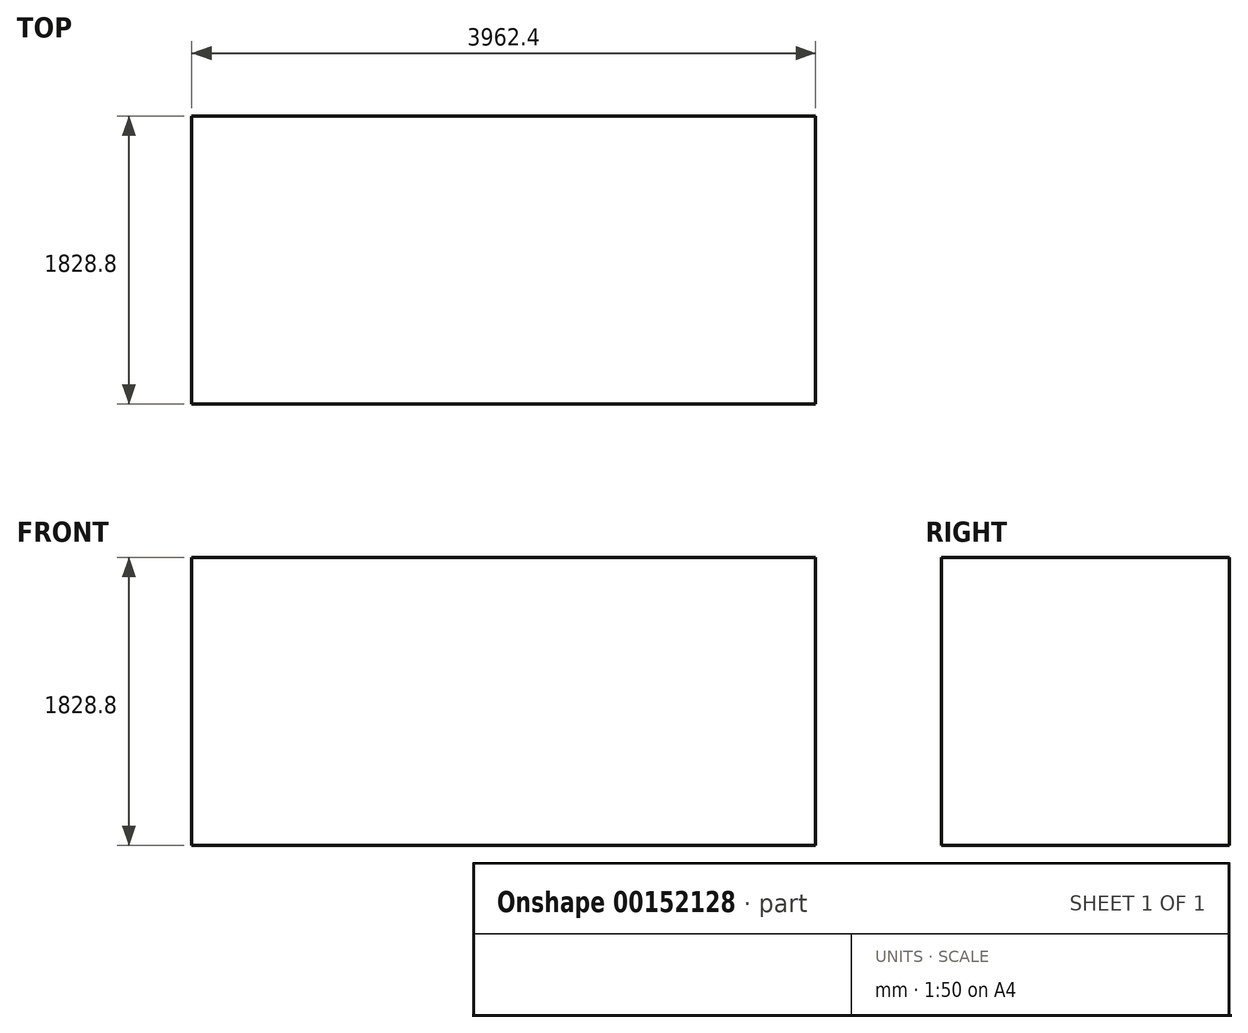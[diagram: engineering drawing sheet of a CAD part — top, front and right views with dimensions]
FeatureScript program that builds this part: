
annotation { "Feature Type Name" : "Feature", "Feature Type Description" : "" }
export const myFeature = defineFeature(function(context is Context, id is Id, definition is map)
    precondition{}
    {
        {
            var Q0;
            Q0=qCreatedBy(makeId("Top.planeOp"),FACE);
            var sketch = newSketch(context, id + "F0", { "sketchPlane" : qUnion([Q0])});
            skLineSegment(sketch, "E0.bottom", {"start": v(1981.2, -914.4) * mm, "end": v(-1981.2, -914.4) * mm});
            skLineSegment(sketch, "E0.top", {"start": v(1981.2, 914.4) * mm, "end": v(-1981.2, 914.4) * mm});
            skLineSegment(sketch, "E0.left", {"start": v(1981.2, -914.4) * mm, "end": v(1981.2, 914.4) * mm});
            skLineSegment(sketch, "E0.right", {"start": v(-1981.2, -914.4) * mm, "end": v(-1981.2, 914.4) * mm});
            skPoint(sketch, "E0.middle", {"position": v(0, 0) * mm});
            skSolve(sketch);
        }
        {
            var Q0;
            Q0 = qSketchRegion(id + "F0", true);
            extrude(context, id + "F1", {"entities" : qUnion([Q0]), "depth" : 1828.8 * mm});
        }
    });
